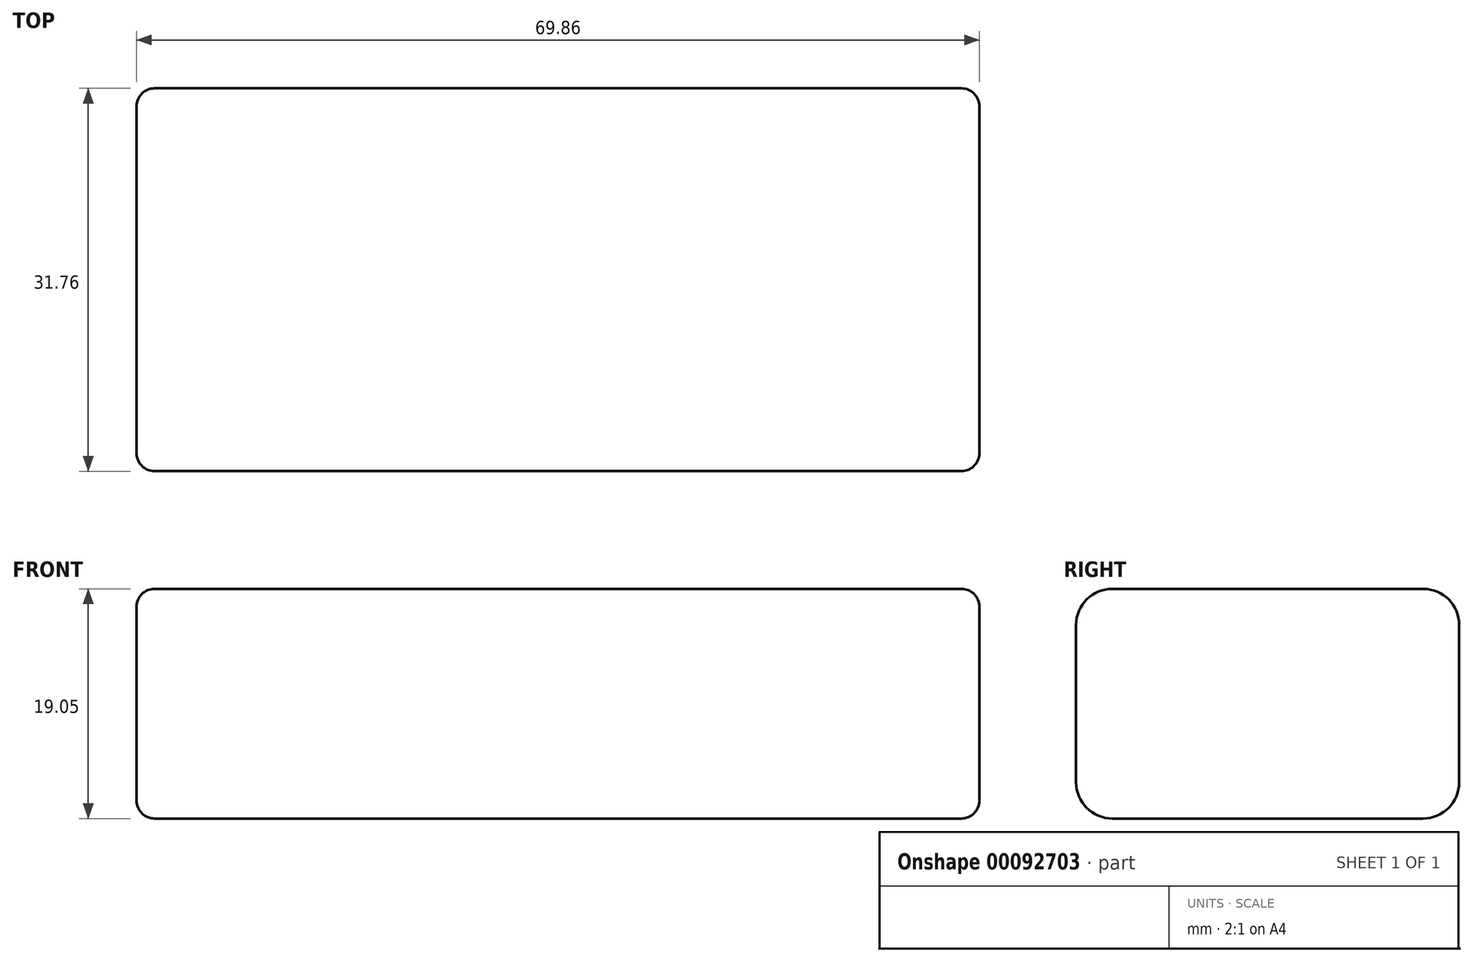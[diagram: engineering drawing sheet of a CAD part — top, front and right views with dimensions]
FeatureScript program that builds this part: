
annotation { "Feature Type Name" : "Feature", "Feature Type Description" : "" }
export const myFeature = defineFeature(function(context is Context, id is Id, definition is map)
    precondition{}
    {
        {
            var Q0;
            Q0=qCreatedBy(makeId("Top.planeOp"),FACE);
            var sketch = newSketch(context, id + "F0", { "sketchPlane" : qUnion([Q0])});
            skLineSegment(sketch, "E0.bottom", {"start": v(-34.93, 15.88) * mm, "end": v(34.93, 15.88) * mm});
            skLineSegment(sketch, "E0.top", {"start": v(-34.93, -15.88) * mm, "end": v(34.93, -15.88) * mm});
            skLineSegment(sketch, "E0.left", {"start": v(-34.93, 15.87) * mm, "end": v(-34.93, -15.88) * mm});
            skLineSegment(sketch, "E0.right", {"start": v(34.93, 15.88) * mm, "end": v(34.93, -15.87) * mm});
            skLineSegment(sketch, "E1", {"start": v(0, 15.88) * mm, "end": v(0, 0) * mm});
            skLineSegment(sketch, "E2", {"start": v(0, 0) * mm, "end": v(-34.93, 0) * mm});
            skSolve(sketch);
        }
        {
            var Q0;
            Q0 = qSketchRegion(id + "F0", true);
            extrude(context, id + "F1", {"entities" : qUnion([Q0]), "depth" : 19.05 * mm});
        }
        {
            var Q0;
            Q0=makeQuery(id+"F1.opExtrude","CAP_EDGE",EDGE,{"disambiguationData":[OSD([sQuery(id+"F0.wireOp",EDGE,"E0.top")])],"isStart":false});
            var Q1;
            Q1=makeQuery(id+"F1.opExtrude","CAP_EDGE",EDGE,{"disambiguationData":[OSD([sQuery(id+"F0.wireOp",EDGE,"E0.top")])],"isStart":true});
            var Q2;
            Q2=makeQuery(id+"F1.opExtrude","CAP_EDGE",EDGE,{"disambiguationData":[OSD([sQuery(id+"F0.wireOp",EDGE,"E0.bottom")])],"isStart":false});
            var Q3;
            Q3=makeQuery(id+"F1.opExtrude","CAP_EDGE",EDGE,{"disambiguationData":[OSD([sQuery(id+"F0.wireOp",EDGE,"E0.bottom")])],"isStart":true});
            fillet(context, id + "F2", {"entities" : qUnion([Q0, Q1, Q2, Q3]), "radius" : 3 * mm, "tangentPropagation" : true, "allowEdgeOverflow" : false});
        }
        {
            var Q0;
            Q0=makeQuery(id+"F1.opExtrude","CAP_EDGE",EDGE,{"disambiguationData":[OSD([sQuery(id+"F0.wireOp",EDGE,"E0.left")])],"isStart":false});
            var Q1;
            Q1=makeQuery(id+"F1.opExtrude","CAP_EDGE",EDGE,{"disambiguationData":[OSD([sQuery(id+"F0.wireOp",EDGE,"E0.right")])],"isStart":false});
            fillet(context, id + "F3", {"entities" : qUnion([Q0, Q1]), "radius" : 1.5 * mm, "tangentPropagation" : true, "allowEdgeOverflow" : false});
        }
    });
